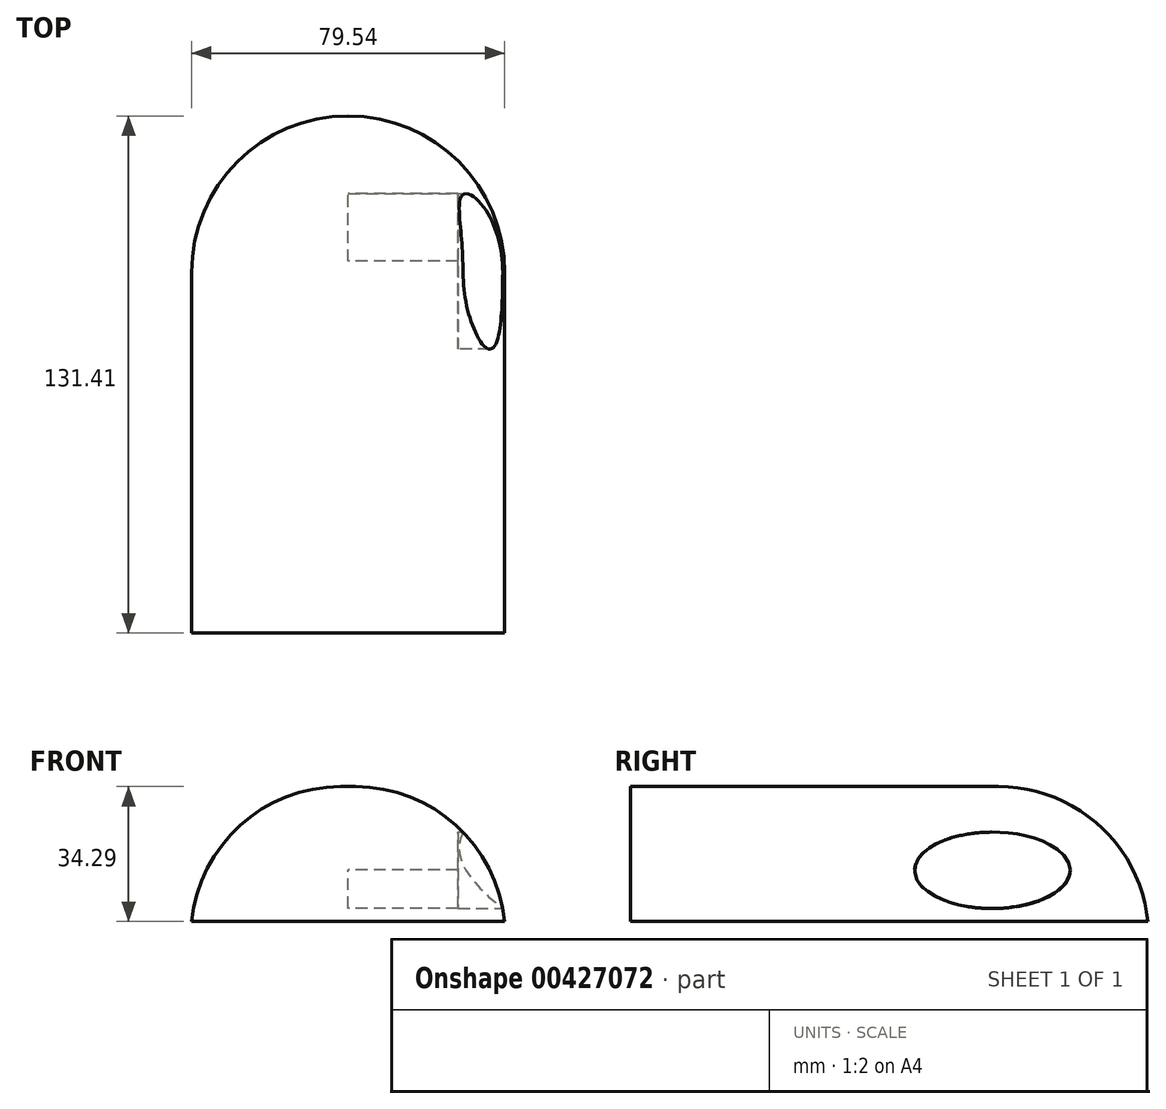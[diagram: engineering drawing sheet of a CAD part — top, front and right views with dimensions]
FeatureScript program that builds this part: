
annotation { "Feature Type Name" : "Feature", "Feature Type Description" : "" }
export const myFeature = defineFeature(function(context is Context, id is Id, definition is map)
    precondition{}
    {
        {
            var Q0;
            Q0=qCreatedBy(makeId("Top.planeOp"),FACE);
            var sketch = newSketch(context, id + "F0", { "sketchPlane" : qUnion([Q0])});
            skLineSegment(sketch, "E0.bottom", {"start": v(39.77, 45.82) * mm, "end": v(-39.77, 45.82) * mm});
            skLineSegment(sketch, "E0.top", {"start": v(39.77, -45.82) * mm, "end": v(-39.77, -45.82) * mm});
            skLineSegment(sketch, "E0.left", {"start": v(39.77, 45.82) * mm, "end": v(39.77, -45.82) * mm});
            skLineSegment(sketch, "E0.right", {"start": v(-39.77, 45.82) * mm, "end": v(-39.77, -45.82) * mm});
            skPoint(sketch, "E0.middle", {"position": v(0, 0) * mm});
            skCircle(sketch, "E1", {"center": v(0, 45.82) * mm, "radius": 39.77 * mm});
            skSolve(sketch);
        }
        {
            var Q0;
            Q0 = qSketchRegion(id + "F0", true);
            extrude(context, id + "F1", {"entities" : qUnion([Q0]), "depth" : 34.3 * mm});
        }
        {
            var Q0;
            Q0=makeQuery(id+"F1.opExtrude","CAP_EDGE",EDGE,{"disambiguationData":[OSD([sQuery(id+"F0.wireOp",EDGE,"E1")])],"isStart":false});
            var Q1;
            Q1=makeQuery(id+"F1.opExtrude","CAP_EDGE",EDGE,{"disambiguationData":[OSD([sQuery(id+"F0.wireOp",EDGE,"E0.right")])],"isStart":false});
            var Q2;
            Q2=makeQuery(id+"F1.opExtrude","CAP_EDGE",EDGE,{"disambiguationData":[OSD([sQuery(id+"F0.wireOp",EDGE,"E0.left")])],"isStart":false});
            fillet(context, id + "F2", {"entities" : qUnion([Q0, Q1, Q2]), "radius" : 38.1 * mm, "allowEdgeOverflow" : false});
        }
        {
            var Q0;
            Q0=qCreatedBy(makeId("Right.planeOp"),FACE);
            var sketch = newSketch(context, id + "F3", { "sketchPlane" : qUnion([Q0])});
            skEllipse(sketch, "E2", {"center": v(46.1, 13.02) * mm, "majorRadius": 19.77 * mm, "minorRadius": 9.7 * mm, "majorAxis": v(-1, 0)});
            skSolve(sketch);
        }
        {
            var Q0;
            Q0 = qSketchRegion(id + "F3", true);
            extrude(context, id + "F4", {"entities" : qUnion([Q0]), "operationType" : NewBodyOperationType.REMOVE, "depth" : 50.8 * mm});
        }
        {
            var Q0;
            Q0=qCreatedBy(makeId("Right.planeOp"),FACE);
            var sketch = newSketch(context, id + "F5", { "sketchPlane" : qUnion([Q0])});
            skEllipse(sketch, "E3", {"center": v(45.17, 13.26) * mm, "majorRadius": 20.7 * mm, "minorRadius": 10 * mm, "majorAxis": v(1, 0)});
            skSolve(sketch);
        }
        {
            var Q0;
            Q0 = qSketchRegion(id + "F5", true);
            extrude(context, id + "F6", {"entities" : qUnion([Q0]), "operationType" : NewBodyOperationType.ADD, "depth" : 27.94 * mm});
        }
    });
